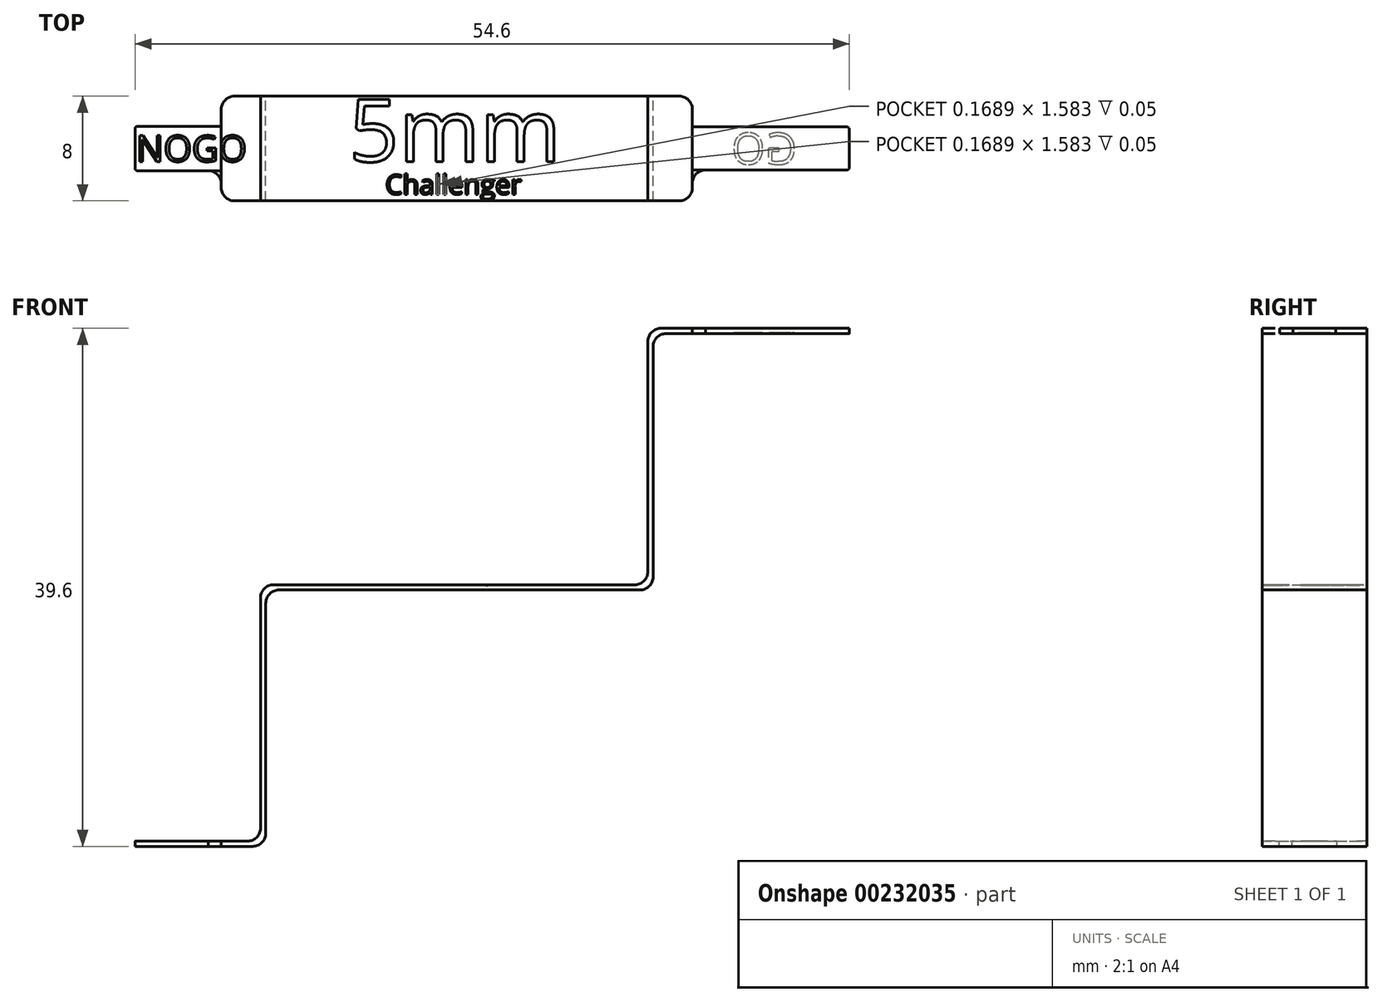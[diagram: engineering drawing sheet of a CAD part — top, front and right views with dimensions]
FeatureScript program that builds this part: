
annotation { "Feature Type Name" : "Feature", "Feature Type Description" : "" }
export const myFeature = defineFeature(function(context is Context, id is Id, definition is map)
    precondition{}
    {
        {
            var Q0;
            Q0=qCreatedBy(makeId("Front.planeOp"),FACE);
            var sketch = newSketch(context, id + "F0", { "sketchPlane" : qUnion([Q0])});
            skLineSegment(sketch, "E0", {"start": v(0, 0) * mm, "end": v(10, 0) * mm});
            skLineSegment(sketch, "E1", {"start": v(10, 0) * mm, "end": v(10, 19.6) * mm});
            skLineSegment(sketch, "E2", {"start": v(10, 19.6) * mm, "end": v(39.6, 19.6) * mm});
            skLineSegment(sketch, "E3", {"start": v(39.6, 19.6) * mm, "end": v(39.6, 39.2) * mm});
            skLineSegment(sketch, "E4", {"start": v(39.6, 39.2) * mm, "end": v(54.6, 39.2) * mm});
            skLineSegment(sketch, "E5", {"start": v(0, 0) * mm, "end": v(0, 0.4) * mm});
            skLineSegment(sketch, "E6", {"start": v(0, 0.4) * mm, "end": v(9.6, 0.4) * mm});
            skLineSegment(sketch, "E7", {"start": v(9.6, 0.4) * mm, "end": v(9.6, 20) * mm});
            skLineSegment(sketch, "E8", {"start": v(9.6, 20) * mm, "end": v(39.2, 20) * mm});
            skLineSegment(sketch, "E9", {"start": v(39.2, 20) * mm, "end": v(39.2, 39.6) * mm});
            skLineSegment(sketch, "E10", {"start": v(39.2, 39.6) * mm, "end": v(54.6, 39.6) * mm});
            skLineSegment(sketch, "E11", {"start": v(54.6, 39.6) * mm, "end": v(54.6, 39.2) * mm});
            skLineSegment(sketch, "E12", {"start": v(6.6, 0.4) * mm, "end": v(6.6, 0) * mm});
            skLineSegment(sketch, "E13", {"start": v(42.6, 39.6) * mm, "end": v(42.6, 39.2) * mm});
            skSolve(sketch);
        }
        {
            var Q0;
            {var subQ0=sQuery(id+"F0.wireOp",EDGE,"E1");Q0=makeQuery(id+"F0.imprint","IMPRINT",FACE,{"disambiguationData":[TD([[makeQuery(id+"F0.imprint","IMPRINT",EDGE,{"derivedFrom":subQ0}),1.0]])]});}
            extrude(context, id + "F1", {"entities" : qUnion([Q0]), "endBound" : BoundingType.SYMMETRIC, "depth" : 8 * mm});
        }
        {
            var Q0;
            {var subQ0=sQuery(id+"F0.wireOp",EDGE,"E5");Q0=makeQuery(id+"F0.imprint","IMPRINT",FACE,{"disambiguationData":[TD([[makeQuery(id+"F0.imprint","IMPRINT",EDGE,{"derivedFrom":subQ0}),-1.0]])]});}
            extrude(context, id + "F2", {"entities" : qUnion([Q0]), "endBound" : BoundingType.SYMMETRIC, "depth" : 3.4 * mm});
        }
        {
            var Q0;
            {var subQ0=sQuery(id+"F0.wireOp",EDGE,"E11");Q0=makeQuery(id+"F0.imprint","IMPRINT",FACE,{"disambiguationData":[TD([[makeQuery(id+"F0.imprint","IMPRINT",EDGE,{"derivedFrom":subQ0}),-1.0]])]});}
            extrude(context, id + "F3", {"entities" : qUnion([Q0]), "endBound" : BoundingType.SYMMETRIC, "depth" : 3.3 * mm});
        }
        {
            var Q0;
            Q0=makeQuery(id+"F1.opExtrude","SWEPT_EDGE",EDGE,{"disambiguationData":[OSD([sQuery(id+"F0.wireOp",EDGE,"E7"),sQuery(id+"F0.wireOp",EDGE,"E8")])]});
            var Q1;
            Q1=makeQuery(id+"F1.opExtrude","SWEPT_EDGE",EDGE,{"disambiguationData":[OSD([sQuery(id+"F0.wireOp",EDGE,"E2"),sQuery(id+"F0.wireOp",EDGE,"E3")])]});
            var Q2;
            Q2=makeQuery(id+"F1.opExtrude","SWEPT_EDGE",EDGE,{"disambiguationData":[OSD([sQuery(id+"F0.wireOp",EDGE,"E8"),sQuery(id+"F0.wireOp",EDGE,"E9")])]});
            var Q3;
            Q3=makeQuery(id+"F1.opExtrude","SWEPT_EDGE",EDGE,{"disambiguationData":[OSD([sQuery(id+"F0.wireOp",EDGE,"E1"),sQuery(id+"F0.wireOp",EDGE,"E2")])]});
            var Q4;
            Q4=makeQuery(id+"F1.opExtrude","SWEPT_EDGE",EDGE,{"disambiguationData":[OSD([sQuery(id+"F0.wireOp",EDGE,"E9"),sQuery(id+"F0.wireOp",EDGE,"E10")])]});
            var Q5;
            Q5=makeQuery(id+"F1.opExtrude","SWEPT_EDGE",EDGE,{"disambiguationData":[OSD([sQuery(id+"F0.wireOp",EDGE,"E0"),sQuery(id+"F0.wireOp",EDGE,"E1")])]});
            var Q6;
            Q6=makeQuery(id+"F1.opExtrude","SWEPT_EDGE",EDGE,{"disambiguationData":[OSD([sQuery(id+"F0.wireOp",EDGE,"E6"),sQuery(id+"F0.wireOp",EDGE,"E7")])]});
            var Q7;
            Q7=makeQuery(id+"F1.opExtrude","SWEPT_EDGE",EDGE,{"disambiguationData":[OSD([sQuery(id+"F0.wireOp",EDGE,"E3"),sQuery(id+"F0.wireOp",EDGE,"E4")])]});
            fillet(context, id + "F4", {"entities" : qUnion([Q0, Q1, Q2, Q3, Q4, Q5, Q6, Q7]), "radius" : 1 * mm, "tangentPropagation" : true, "allowEdgeOverflow" : false});
        }
        {
            var Q0;
            Q0=makeQuery(id+"F1.opExtrude","CAP_EDGE",EDGE,{"disambiguationData":[OSD([sQuery(id+"F0.wireOp",EDGE,"E12")])],"isStart":true});
            var Q1;
            Q1=makeQuery(id+"F1.opExtrude","CAP_EDGE",EDGE,{"disambiguationData":[OSD([sQuery(id+"F0.wireOp",EDGE,"E12")])],"isStart":false});
            var Q2;
            Q2=makeQuery(id+"F1.opExtrude","CAP_EDGE",EDGE,{"disambiguationData":[OSD([sQuery(id+"F0.wireOp",EDGE,"E13")])],"isStart":false});
            var Q3;
            Q3=makeQuery(id+"F1.opExtrude","CAP_EDGE",EDGE,{"disambiguationData":[OSD([sQuery(id+"F0.wireOp",EDGE,"E13")])],"isStart":true});
            fillet(context, id + "F5", {"entities" : qUnion([Q0, Q1, Q2, Q3]), "radius" : 1 * mm, "tangentPropagation" : true, "allowEdgeOverflow" : false});
        }
        {
            var Q0;
            Q0=makeQuery(id+"F2.opExtrude","CAP_EDGE",EDGE,{"disambiguationData":[OSD([sQuery(id+"F0.wireOp",EDGE,"E5")])],"isStart":true});
            var Q1;
            Q1=makeQuery(id+"F2.opExtrude","CAP_EDGE",EDGE,{"disambiguationData":[OSD([sQuery(id+"F0.wireOp",EDGE,"E5")])],"isStart":false});
            var Q2;
            Q2=makeQuery(id+"F3.opExtrude","CAP_EDGE",EDGE,{"disambiguationData":[OSD([sQuery(id+"F0.wireOp",EDGE,"E11")])],"isStart":true});
            var Q3;
            Q3=makeQuery(id+"F3.opExtrude","CAP_EDGE",EDGE,{"disambiguationData":[OSD([sQuery(id+"F0.wireOp",EDGE,"E11")])],"isStart":false});
            fillet(context, id + "F6", {"entities" : qUnion([Q0, Q1, Q2, Q3]), "radius" : 0.2 * mm, "tangentPropagation" : true, "allowEdgeOverflow" : false});
        }
        {
            var Q0;
            Q0=makeQuery(id+"F2.opExtrude","SWEPT_FACE",FACE,{"disambiguationData":[OSD([sQuery(id+"F0.wireOp",EDGE,"E6")])]});
            var sketch = newSketch(context, id + "F7", { "sketchPlane" : qUnion([Q0])});
            skText(sketch, "E14", { "text": "NOGO\n\n", "fontName": "OpenSans-Regular.ttf"});
            const initialGuessF7  = {"E14": [0.0001, -0.001, 1, 0, 0.002]};
            skSetInitialGuess(sketch, initialGuessF7);
            skSolve(sketch);
        }
        {
            var Q0;
            Q0=makeQuery(id+"F3.opExtrude","SWEPT_FACE",FACE,{"disambiguationData":[OSD([sQuery(id+"F0.wireOp",EDGE,"E4")])]});
            var sketch = newSketch(context, id + "F8", { "sketchPlane" : qUnion([Q0])});
            skSolve(sketch);
        }
        {
            var Q0;
            Q0=makeQuery(id+"F1.opExtrude","SWEPT_FACE",FACE,{"disambiguationData":[OSD([sQuery(id+"F0.wireOp",EDGE,"E6")])]});
            var sketch = newSketch(context, id + "F9", { "sketchPlane" : qUnion([Q0])});
            skArc(sketch, "E15", {"start": v(6.6, 2.7) * mm, "mid": v(6.3, 2) * mm, "end": v(5.6, 1.7) * mm});
            skArc(sketch, "E16", {"start": v(6.6, -2.7) * mm, "mid": v(6.3, -2) * mm, "end": v(5.6, -1.7) * mm});
            skLineSegment(sketch, "E17", {"start": v(6.6, 2.7) * mm, "end": v(6.6, 1.7) * mm});
            skLineSegment(sketch, "E18", {"start": v(6.6, 1.7) * mm, "end": v(5.6, 1.7) * mm});
            skLineSegment(sketch, "E19", {"start": v(5.6, -1.7) * mm, "end": v(6.6, -1.7) * mm});
            skLineSegment(sketch, "E20", {"start": v(6.6, -1.7) * mm, "end": v(6.6, -2.7) * mm});
            skSolve(sketch);
        }
        {
            var Q0;
            Q0=makeQuery(id+"F9.imprint","IMPRINT",FACE,{"disambiguationData":[TD([[makeQuery(id+"F9.imprint","IMPRINT",EDGE,{"derivedFrom":sQuery(id+"F9.wireOp",EDGE,"E15")}),1.0]])]});
            var Q1;
            Q1=makeQuery(id+"F9.imprint","IMPRINT",FACE,{"disambiguationData":[TD([[makeQuery(id+"F9.imprint","IMPRINT",EDGE,{"derivedFrom":sQuery(id+"F9.wireOp",EDGE,"E16")}),-1.0]])]});
            extrude(context, id + "F10", {"entities" : qUnion([Q0, Q1]), "oppositeDirection" : true, "depth" : 0.4 * mm});
        }
        {
            var Q0;
            Q0=makeQuery(id+"F3.opExtrude","SWEPT_FACE",FACE,{"disambiguationData":[OSD([sQuery(id+"F0.wireOp",EDGE,"E10")])]});
            var sketch = newSketch(context, id + "F11", { "sketchPlane" : qUnion([Q0])});
            skArc(sketch, "E21", {"start": v(43.6, 1.65) * mm, "mid": v(42.9, 1.94) * mm, "end": v(42.6, 2.65) * mm});
            skArc(sketch, "E22", {"start": v(43.6, -1.65) * mm, "mid": v(42.9, -1.94) * mm, "end": v(42.6, -2.65) * mm});
            skLineSegment(sketch, "E23", {"start": v(42.6, 2.65) * mm, "end": v(42.6, 1.65) * mm});
            skLineSegment(sketch, "E24", {"start": v(42.6, 1.65) * mm, "end": v(43.6, 1.65) * mm});
            skLineSegment(sketch, "E25", {"start": v(43.6, -1.65) * mm, "end": v(42.6, -1.65) * mm});
            skLineSegment(sketch, "E26", {"start": v(42.6, -1.65) * mm, "end": v(42.6, -2.65) * mm});
            skSolve(sketch);
        }
        {
            var Q0;
            Q0=makeQuery(id+"F11.imprint","IMPRINT",FACE,{"disambiguationData":[TD([[makeQuery(id+"F11.imprint","IMPRINT",EDGE,{"derivedFrom":sQuery(id+"F11.wireOp",EDGE,"E21")}),1.0]])]});
            var Q1;
            Q1=makeQuery(id+"F11.imprint","IMPRINT",FACE,{"disambiguationData":[TD([[makeQuery(id+"F11.imprint","IMPRINT",EDGE,{"derivedFrom":sQuery(id+"F11.wireOp",EDGE,"E22")}),-1.0]])]});
            extrude(context, id + "F12", {"entities" : qUnion([Q0, Q1]), "oppositeDirection" : true, "depth" : 0.4 * mm});
        }
        {
            var Q0;
            Q0=makeQuery(id+"F7.imprint","IMPRINT",FACE,{"disambiguationData":[TD([[makeQuery(id+"F7.imprint","IMPRINT",EDGE,{"derivedFrom":sQuery(id+"F7.wireOp",EDGE,"E14.sketch_text.stroke-15")}),-1.0]])]});
            var Q1;
            Q1=makeQuery(id+"F7.imprint","IMPRINT",FACE,{"disambiguationData":[TD([[makeQuery(id+"F7.imprint","IMPRINT",EDGE,{"derivedFrom":sQuery(id+"F7.wireOp",EDGE,"E14.sketch_text.stroke-31")}),-1.0]])]});
            var Q2;
            Q2=makeQuery(id+"F7.imprint","IMPRINT",FACE,{"disambiguationData":[TD([[makeQuery(id+"F7.imprint","IMPRINT",EDGE,{"derivedFrom":sQuery(id+"F7.wireOp",EDGE,"E14.sketch_text.stroke-51")}),-1.0]])]});
            var Q3;
            Q3=makeQuery(id+"F7.imprint","IMPRINT",FACE,{"disambiguationData":[TD([[makeQuery(id+"F7.imprint","IMPRINT",EDGE,{"derivedFrom":sQuery(id+"F7.wireOp",EDGE,"E14.sketch_text.stroke-0")}),-1.0]])]});
            var Q4;
            {var subQ4=sQuery(id+"F7.wireOp",EDGE,"E14.sketch_text.stroke-53");Q4=makeQuery(id+"F7.imprint","IMPRINT",FACE,{"disambiguationData":[TD([[makeQuery(id+"F7.imprint","IMPRINT",EDGE,{"derivedFrom":subQ4}),-1.0]])]});}
            extrude(context, id + "F13", {"entities" : qUnion([Q0, Q1, Q2, Q3, Q4]), "operationType" : NewBodyOperationType.REMOVE, "oppositeDirection" : true, "depth" : 0.01 * mm});
        }
        {
            var Q0;
            Q0=makeQuery(id+"F1.opExtrude","SWEPT_FACE",FACE,{"disambiguationData":[OSD([sQuery(id+"F0.wireOp",EDGE,"E8")])]});
            var sketch = newSketch(context, id + "F14", { "sketchPlane" : qUnion([Q0])});
            skText(sketch, "E27", { "text": "5mm", "fontName": "OpenSans-Regular.ttf"});
            skLineSegment(sketch, "E28", {"start": v(10.6, 4) * mm, "end": v(38.2, 4) * mm});
            skPoint(sketch, "E29", {"position": v(24.4, 4) * mm});
            skPoint(sketch, "E30", {"position": v(24.4, 3.8) * mm});
            skText(sketch, "E31", { "text": "Challenger", "fontName": "OpenSans-Regular.ttf"});
            skLineSegment(sketch, "E32", {"start": v(24.4, -1) * mm, "end": v(24.4, -2) * mm, "construction": true});
            const initialGuessF14  = {"E27": [0.01635, -0.001, 1, 0, 0.0048], "E31": [0.01914, -0.0035, 1, 0, 0.0015]};
            skSetInitialGuess(sketch, initialGuessF14);
            skSolve(sketch);
        }
        {
            var Q0;
            Q0=makeQuery(id+"F14.imprint","IMPRINT",FACE,{"disambiguationData":[TD([[makeQuery(id+"F14.imprint","IMPRINT",EDGE,{"derivedFrom":sQuery(id+"F14.wireOp",EDGE,"E27.sketch_text.stroke-0")}),-1.0]])]});
            var Q1;
            Q1=makeQuery(id+"F14.imprint","IMPRINT",FACE,{"disambiguationData":[TD([[makeQuery(id+"F14.imprint","IMPRINT",EDGE,{"derivedFrom":sQuery(id+"F14.wireOp",EDGE,"E27.sketch_text.stroke-19")}),-1.0]])]});
            var Q2;
            Q2=makeQuery(id+"F14.imprint","IMPRINT",FACE,{"disambiguationData":[TD([[makeQuery(id+"F14.imprint","IMPRINT",EDGE,{"derivedFrom":sQuery(id+"F14.wireOp",EDGE,"E27.sketch_text.stroke-47")}),-1.0]])]});
            extrude(context, id + "F15", {"entities" : qUnion([Q0, Q1, Q2]), "operationType" : NewBodyOperationType.REMOVE, "oppositeDirection" : true, "depth" : 0.05 * mm});
        }
        {
            var Q0;
            {var subQ0=sQuery(id+"F0.wireOp",EDGE,"E4");Q0=makeQuery(id+"F8.imprint","IMPRINT",FACE,{"disambiguationData":[TD([[makeQuery(id+"F8.imprint","IMPRINT",EDGE,{"derivedFrom":makeQuery(id+"F3.opExtrude","CAP_EDGE",EDGE,{"disambiguationData":[OSD([subQ0])],"isStart":true})}),1.0]])]});}
            var sketch = newSketch(context, id + "F16", { "sketchPlane" : qUnion([Q0])});
            skText(sketch, "E33", { "text": "GO", "fontName": "OpenSans-Regular.ttf"});
            skPoint(sketch, "E34", {"position": v(50.6, 1.2) * mm});
            const initialGuessF16  = {"E33": [0.0506, 0.0012, -1, 0, 0.0024]};
            skSetInitialGuess(sketch, initialGuessF16);
            skSolve(sketch);
        }
        {
            var Q0;
            Q0 = qSketchRegion(id + "F16", true);
            extrude(context, id + "F17", {"entities" : qUnion([Q0]), "operationType" : NewBodyOperationType.REMOVE, "oppositeDirection" : true, "depth" : 0.05 * mm});
        }
        {
            var Q0;
            Q0=makeQuery(id+"F14.imprint","IMPRINT",FACE,{"disambiguationData":[TD([[makeQuery(id+"F14.imprint","IMPRINT",EDGE,{"derivedFrom":sQuery(id+"F14.wireOp",EDGE,"E31.sketch_text.stroke-0")}),-1.0]])]});
            var Q1;
            Q1=makeQuery(id+"F14.imprint","IMPRINT",FACE,{"disambiguationData":[TD([[makeQuery(id+"F14.imprint","IMPRINT",EDGE,{"derivedFrom":sQuery(id+"F14.wireOp",EDGE,"E31.sketch_text.stroke-15")}),-1.0]])]});
            var Q2;
            Q2=makeQuery(id+"F14.imprint","IMPRINT",FACE,{"disambiguationData":[TD([[makeQuery(id+"F14.imprint","IMPRINT",EDGE,{"derivedFrom":sQuery(id+"F14.wireOp",EDGE,"E31.sketch_text.stroke-33")}),-1.0]])]});
            var Q3;
            Q3=makeQuery(id+"F14.imprint","IMPRINT",FACE,{"disambiguationData":[TD([[makeQuery(id+"F14.imprint","IMPRINT",EDGE,{"derivedFrom":sQuery(id+"F14.wireOp",EDGE,"E31.sketch_text.stroke-60")}),-1.0]])]});
            var Q4;
            Q4=makeQuery(id+"F14.imprint","IMPRINT",FACE,{"disambiguationData":[TD([[makeQuery(id+"F14.imprint","IMPRINT",EDGE,{"derivedFrom":sQuery(id+"F14.wireOp",EDGE,"E31.sketch_text.stroke-64")}),-1.0]])]});
            var Q5;
            Q5=makeQuery(id+"F14.imprint","IMPRINT",FACE,{"disambiguationData":[TD([[makeQuery(id+"F14.imprint","IMPRINT",EDGE,{"derivedFrom":sQuery(id+"F14.wireOp",EDGE,"E31.sketch_text.stroke-68")}),-1.0]])]});
            var Q6;
            Q6=makeQuery(id+"F14.imprint","IMPRINT",FACE,{"disambiguationData":[TD([[makeQuery(id+"F14.imprint","IMPRINT",EDGE,{"derivedFrom":sQuery(id+"F14.wireOp",EDGE,"E31.sketch_text.stroke-87")}),-1.0]])]});
            var Q7;
            Q7=makeQuery(id+"F14.imprint","IMPRINT",FACE,{"disambiguationData":[TD([[makeQuery(id+"F14.imprint","IMPRINT",EDGE,{"derivedFrom":sQuery(id+"F14.wireOp",EDGE,"E31.sketch_text.stroke-104")}),-1.0]])]});
            var Q8;
            Q8=makeQuery(id+"F14.imprint","IMPRINT",FACE,{"disambiguationData":[TD([[makeQuery(id+"F14.imprint","IMPRINT",EDGE,{"derivedFrom":sQuery(id+"F14.wireOp",EDGE,"E31.sketch_text.stroke-148")}),-1.0]])]});
            var Q9;
            Q9=makeQuery(id+"F14.imprint","IMPRINT",FACE,{"disambiguationData":[TD([[makeQuery(id+"F14.imprint","IMPRINT",EDGE,{"derivedFrom":sQuery(id+"F14.wireOp",EDGE,"E31.sketch_text.stroke-167")}),-1.0]])]});
            extrude(context, id + "F18", {"entities" : qUnion([Q0, Q1, Q2, Q3, Q4, Q5, Q6, Q7, Q8, Q9]), "operationType" : NewBodyOperationType.REMOVE, "oppositeDirection" : true, "depth" : 0.05 * mm});
        }
        {
            var Q0;
            {var subQ2=sQuery(id+"F7.wireOp",EDGE,"E14.sketch_text.stroke-51");Q0=makeQuery(id+"F7.imprint","IMPRINT",FACE,{"disambiguationData":[TD([[makeQuery(id+"F7.imprint","IMPRINT",EDGE,{"derivedFrom":subQ2}),-1.0]])]});}
            extrude(context, id + "F19", {"entities" : qUnion([Q0]), "operationType" : NewBodyOperationType.REMOVE, "oppositeDirection" : true, "depth" : 0.01 * mm});
        }
    });
